# Revit family: HVAC_HeatPumpAW_Enertech_CTC-EcoAir-622M
name_source: partatom
category: Specialty Equipment
units: mm (PartAtom-declared; Revit-internal decimal feet)

## family parameters
Always vertical = Yes
Cut with Voids When Loaded = No
OmniClass Number = 23.75.00.00
OmniClass Title = Climate Control (HVAC)
Part Type = Normal
Room Calculation Point = No
Round Connector Dimension = Use Diameter
Shared = No
Work Plane-Based = No

## types (1)
- CTC EcoAir 622M
    AirFlow max (m3/h) = 5457
    AirFlow nominal (m3/h) = 4200
    AssetType = Fixed
    BIMObjectName = HVAC_HeatPumpAW_Enertech_CTC-EcoAir-622M
    Brand = CTC
    CO2Equivalent = 4.790
    COP max: W35 & A +12 = 3.51
    COP max: W35 & A +2 = 2.60
    COP max: W35 & A +7 = 2.92
    COP max: W35 & A -15 = 2.01
    COP max: W35 & A -7 = 2.32
    COP min: W35 & A +12 = 5.65
    COP min: W35 & A +2 = 3.67
    COP min: W35 & A +7 = 5.07
    COP min: W35 & A -15 = 0
    COP min: W35 & A -7 = 0
    Capacity = Variable
    Category = Heat Pumps, Air-to-water
    Color = grey
    CoolingCapacity max: A35 & W18 = 13000 W
    CoolingCapacity max: A35 & W7 = 13000 W
    CoolingCapacity min: A35 & W18 = 13000 W
    CoolingCapacity min: A35 & W7 = 12000 W
    CoolingCapacity nominal: A35 & W18 = 9000 W
    CoolingCapacity nominal: A35 & W7 = 9000 W
    Cost = 0 $
    Default Elevation = 0 mm  [stored 0 ft]
    Description = CTC EcoAir 622M a speed controlled air-to-water heat pump,  which automatically adapts to the building's power demand during the year.
    DurationUnit = Year
    EANNumber = 7333077087661
    EER max: A35 & W18 = 0
    EER max: A35 & W7 = 0
    EER min: A35 & W18 = 0
    EER min: A35 & W7 = 0
    EER nominal: A35 & W18 = 0
    EER nominal: A35 & W7 = 0
    ElectricalDeviceNominalPower = 0 W
    EnergyClassHeatingWithControl W35 = A+++
    EnergyClassHeatingWithControl W55 = A+++
    EnergyClassHeatingWithoutControl W35 = A+++
    EnergyClassHeatingWithoutControl W55 = A++
    GroupFuse = 20
    HasProtectiveEarth = Yes
    IP_Code = IP X4
    IfcExportAs = IfcElectricalDeviceCommon
    IfcExportType = HEATER
    InPutPower max: W35 & A +12 = 6980 W
    InPutPower max: W35 & A +2 = 5910 W
    InPutPower max: W35 & A +7 = 6350 W
    InPutPower max: W35 & A -15 = 5990 W
    InPutPower max: W35 & A -7 = 6030 W
    InPutPower min: W35 & A +12 = 970 W
    InPutPower min: W35 & A +2 = 1010 W
    InPutPower min: W35 & A +7 = 940 W
    InPutPower min: W35 & A -15 = 0 W
    InPutPower min: W35 & A -7 = 0 W
    KvsValueProduct = 7.7
    Manufacturer = CTC AB
    ManufacturerCountry = Sweden
    ManufacturerName = CTC AB
    ManufacturerURL = https://ctc.se
    Material = Steel
    MaxOperatingPressureThermalStore = 3
    MaxStartingCurrent = 4.9
    Model = CTC EcoAir 622M
    ModelNumber = 588401001
    NBSDescription = Air to water heat pumps
    NBSReference = 90-40-40/320
    Name = CTC-EcoAir-600M
    NominalCurrent = 0 A
    NominalDepth = 645 mm
    NominalFrequencyRange = 50 Hz
    NominalHeight = 1180 mm  [stored 3.87139 ft]
    NominalVoltage = 400 V
    NominalWidth = 1375 mm  [stored 4.51115 ft]
    NumberOfPoles = 3
    PhaseAngle = 0.00°
    PowerFactor = 0 W
    ProductInformation = CTC EcoAir 622M a speed controlled air-to-water heat pump,  which automatically adapts to the building's power demand during the year.
    PumpMainMaterial = Steel - Grey
    RatedCurrent = 17 A
    RatedHeatOutputCold Pdesigh W35 = 0 W
    RatedHeatOutputCold Pdesigh W55 = 0 W
    RatedHeatOutputModerate Pdesigh W35 = 0 W
    RatedHeatOutputModerate Pdesigh W55 = 0 W
    RatedHeatOutputWarm Pdesigh W35 = 0 W
    RatedHeatOutputWarm Pdesigh W55 = 0 W
    RatedVoltage = 1200 V
    RefrigerantQuantity = 2.7
    RefrigerantType = R407C
    Revision = 6
    SCOPCold W35 = 4.26
    SCOPCold W55 = 3.47
    SCOPModerate W35 = 4.92
    SCOPModerate W55 = 3.77
    SCOPWarm W35 = 6.19
    SCOPWarm W55 = 4.64
    Shape = Rectangular
    Size = 645x1375x1180
    Sound pressureLPA 10m = 30
    Sound pressureLPA 5m = 36
    SoundPowerLWA = 55
    SpecifiedOutput max: W35 & A +12 = 24470 W
    SpecifiedOutput max: W35 & A +2 = 15390 W
    SpecifiedOutput max: W35 & A +7 = 18510 W
    SpecifiedOutput max: W35 & A -15 = 12050 W
    SpecifiedOutput max: W35 & A -7 = 13990 W
    SpecifiedOutput min: W35 & A +12 = 5480 W
    SpecifiedOutput min: W35 & A +2 = 3720 W
    SpecifiedOutput min: W35 & A +7 = 4740 W
    SpecifiedOutput min: W35 & A -15 = 0 W
    SpecifiedOutput min: W35 & A -7 = 0 W
    Touchscreen = no
    UNSPSCCode = 40101806
    URL = https://ctc-heating.com
    Uniclass2 = Pr_40_70_65
    Uniclass2015Description = Preparation catering equipment
    Uniclass2015Reference = Pr_40_70_65
    UsageCurrent = 0 A
    Version = 6
    VersionDate = 13/05/2024
    WarrantyDurationUnit = Year
    WaterVolumeHeathingSystem = 2.8
    Weight = 192

note: [stored X ft] marks values corroborated as IEEE doubles in the binary element streams (Revit-internal decimal feet)

## geometry (parser evidence)
native form markers: Sweep x5
no freeform markers — native parametric forms only
